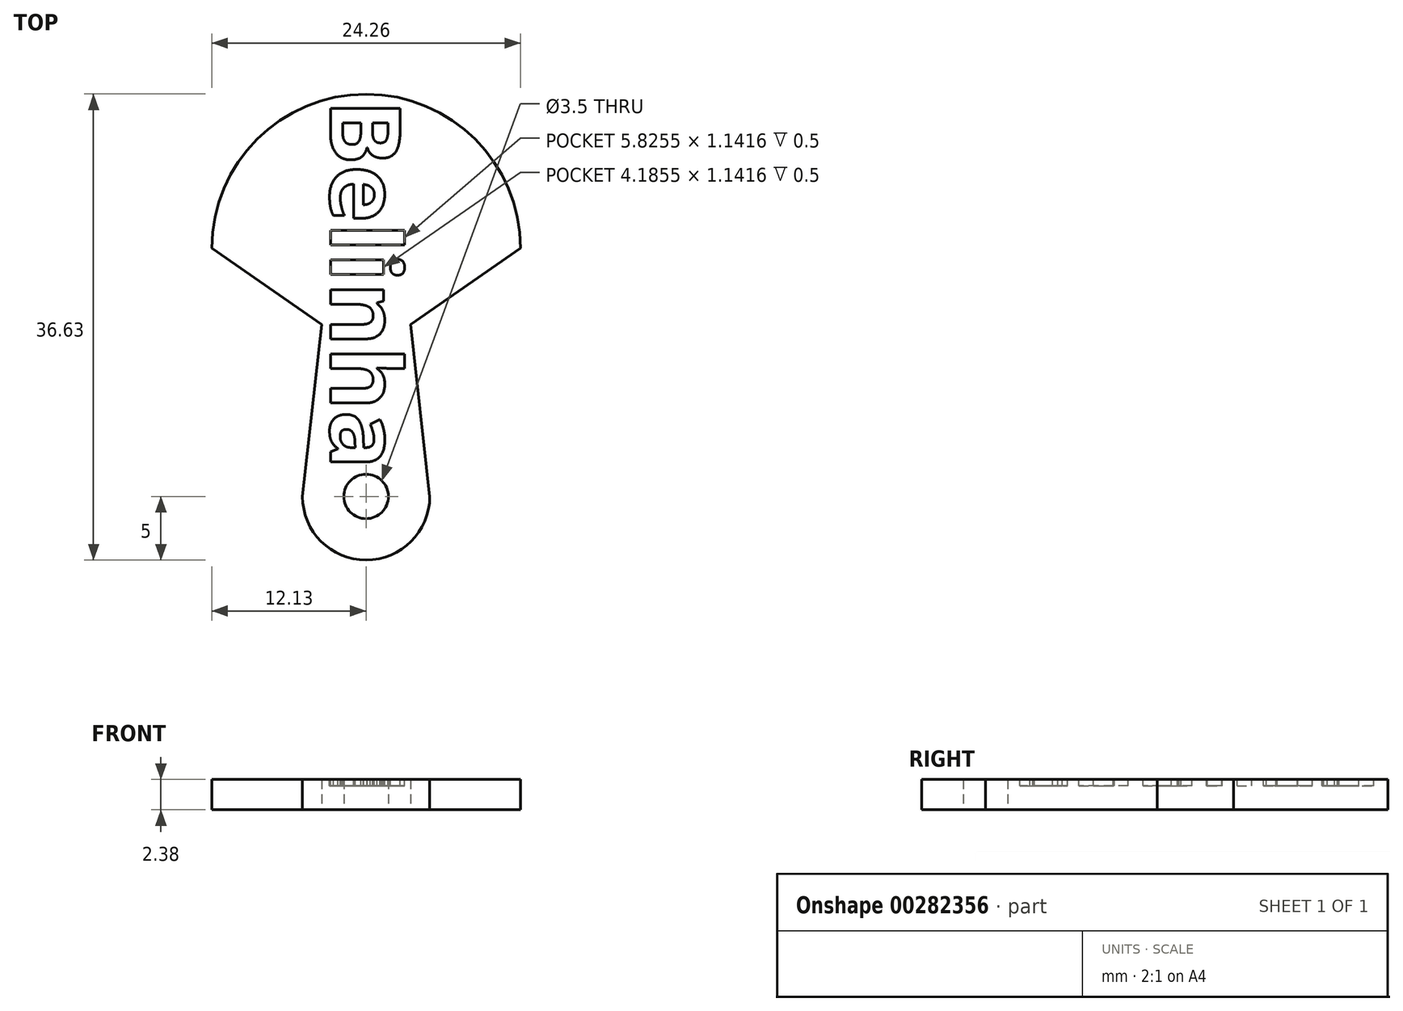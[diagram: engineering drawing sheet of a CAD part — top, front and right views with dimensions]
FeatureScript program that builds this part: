
annotation { "Feature Type Name" : "Feature", "Feature Type Description" : "" }
export const myFeature = defineFeature(function(context is Context, id is Id, definition is map)
    precondition{}
    {
        {
            var Q0;
            Q0=qCreatedBy(makeId("Top.planeOp"),FACE);
            var sketch = newSketch(context, id + "F0", { "sketchPlane" : qUnion([Q0])});
            skArc(sketch, "E0", {"start": v(12.12, 0) * mm, "mid": v(0, 12.12) * mm, "end": v(-12.12, 0) * mm});
            skArc(sketch, "E1", {"start": v(-5, -19.5) * mm, "mid": v(0, -24.5) * mm, "end": v(5, -19.5) * mm});
            skLineSegment(sketch, "E2", {"start": v(-5, -19.5) * mm, "end": v(-3.5, -6) * mm});
            skLineSegment(sketch, "E3", {"start": v(5, -19.5) * mm, "end": v(3.5, -6) * mm});
            skLineSegment(sketch, "E4", {"start": v(-3.5, -6) * mm, "end": v(-12.13, 0) * mm});
            skLineSegment(sketch, "E5", {"start": v(3.5, -6) * mm, "end": v(12.12, 0) * mm});
            skCircle(sketch, "E6", {"center": v(0, -19.5) * mm, "radius": 1.75 * mm});
            skSolve(sketch);
        }
        {
            var Q0;
            Q0 = qSketchRegion(id + "F0", true);
            extrude(context, id + "F1", {"entities" : qUnion([Q0]), "depth" : 2.38 * mm});
        }
        {
            var Q0;
            Q0=makeQuery(id+"F1.opExtrude","CAP_FACE",FACE,{"disambiguationData":[OSD([sQuery(id+"F0.wireOp",EDGE,"E0"),sQuery(id+"F0.wireOp",EDGE,"E1"),sQuery(id+"F0.wireOp",EDGE,"E2"),sQuery(id+"F0.wireOp",EDGE,"E3"),sQuery(id+"F0.wireOp",EDGE,"E4"),sQuery(id+"F0.wireOp",EDGE,"E5"),sQuery(id+"F0.wireOp",EDGE,"E6")])],"isStart":false});
            var sketch = newSketch(context, id + "F2", { "sketchPlane" : qUnion([Q0])});
            skText(sketch, "E7", { "text": "Belinha", "fontName": "OpenSans-Bold.ttf"});
            const initialGuessF2  = {"E7": [-0.0028, 0.0117, 0, -1, 0.00552]};
            skSetInitialGuess(sketch, initialGuessF2);
            skSolve(sketch);
        }
        {
            var Q0;
            Q0 = qSketchRegion(id + "F2", true);
            extrude(context, id + "F3", {"entities" : qUnion([Q0]), "operationType" : NewBodyOperationType.REMOVE, "oppositeDirection" : true, "depth" : 0.5 * mm});
        }
    });
